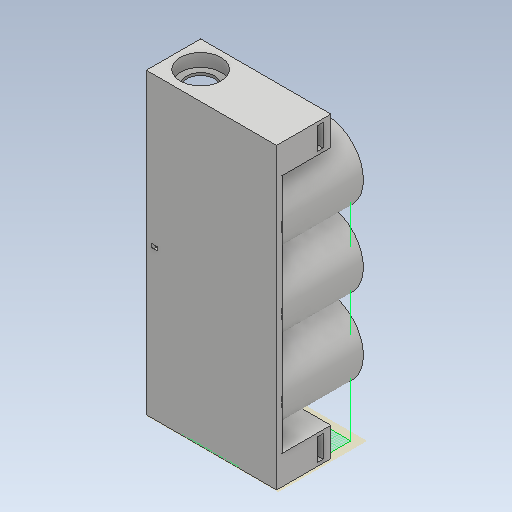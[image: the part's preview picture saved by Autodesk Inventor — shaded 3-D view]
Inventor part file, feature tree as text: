
AUTODESK INVENTOR PART (.ipt)
format: ipt  version: 2020 (Build 240168000, 168)  size: 739,328 bytes
history: native  units: mm
features: sketch x25, extrude x22, fillet x4
ambient origin geometry x8: Origin, YZ Plane, XZ Plane, XY Plane, X Axis, Y Axis, Z Axis, Center Point
bodies: Solid1 (feature_tree)
feature tree (51):
  extrude  "Extrusion1"  Depth=165.0mm
  extrude  "Extrusion2"  Depth=8.5mm
  extrude  "Extrusion3"  Depth=25.0mm TaperAngle=0.0deg
  extrude  "Extrusion4"  Depth=22.75mm
  extrude  "Extrusion5"  Depth=15.5mm
  extrude  "Extrusion6"  Depth=7.1mm TaperAngle=0.0deg
  fillet  "Fillet1"  Radius=5.0mm
  extrude  "Extrusion7"  Depth=10.0mm TaperAngle=0.0deg
  fillet  "Fillet2"  Radius=2.0mm
  extrude  "Extrusion8"  Depth=16.0mm
  extrude  "Extrusion9"  Depth=16.0mm
  fillet  "Fillet3"  Radius=8.0mm
  extrude  "Extrusion10"  Depth=6.0mm
  extrude  "Extrusion11"  Depth=12.25mm
  sketch  "Sketch12"  dims[d32=12.25mm d33=3.5mm]
  sketch  "Sketch13"  dims[d34=12.25mm d35=12.25mm]
  extrude  "Extrusion12"  Depth=12.25mm
  extrude  "Extrusion13"  Depth=12.25mm
  sketch  "Sketch16"  dims[d41=8.0mm d42=1.0mm]
  extrude  "Extrusion14"  Depth=40.0mm TaperAngle=0.0deg
  extrude  "Extrusion15"  Depth=2.0mm
  extrude  "Extrusion16"  Depth=1.0mm
  extrude  "Extrusion17"  Depth=2.0mm TaperAngle=0.0deg
  extrude  "Extrusion18"  Depth=7.1mm TaperAngle=0.0deg
  fillet  "Fillet4"  Radius=3.0mm
  extrude  "Extrusion19"  Depth=42.0mm
  extrude  "Extrusion20"  Depth=42.0mm
  extrude  "Extrusion21"  Depth=42.0mm
  extrude  "Extrusion22"  Depth=2.0mm
  sketch  "Sketch1"  dims[d0=25.0mm d1=165.0mm]
  sketch  "Sketch2"  dims[d2=3.0mm d3=0.0mm d4=8.5mm]
  sketch  "Sketch3"  dims[d5=8.5mm d6=25.0mm d7=0.0mm]
  sketch  "Sketch4"  dims[d8=25.0mm d9=22.75mm]
  sketch  "Sketch5"  dims[d10=7.1mm d11=0.0mm d12=15.5mm]
  sketch  "Sketch6"  dims[d13=165.0mm d14=0.0mm d15=7.1mm d16=0.0mm d17=5.0mm]
  sketch  "Sketch7"  dims[d18=5.0mm d19=10.0mm d20=0.0mm d21=2.0mm]
  sketch  "Sketch8"  dims[d22=16.0mm d23=8.0mm]
  sketch  "Sketch9"  dims[d24=16.0mm d25=16.0mm d26=8.0mm]
  sketch  "Sketch10"  dims[d27=45.0mm d28=0.0mm d29=6.0mm]
  sketch  "Sketch11"  dims[d30=12.25mm d31=3.5mm]
  sketch  "Sketch14"  dims[d36=3.5mm d37=40.0mm d38=0.0mm]
  sketch  "Sketch15"  dims[d39=1.0mm d40=2.0mm]
  sketch  "Sketch17"  dims[d43=2.0mm d44=12.0mm d45=0.0mm]
  sketch  "Sketch18"  dims[d46=6.0mm d47=7.1mm d48=0.0mm d49=3.0mm d50=0.0mm]
  sketch  "Sketch19"  dims[d51=42.0mm d52=38.75mm]
  sketch  "Sketch20"  dims[d53=42.0mm d54=38.75mm]
  sketch  "Sketch21"  dims[d55=42.0mm d56=38.75mm]
  sketch  "Sketch22"  dims[d57=45.0mm d58=0.0mm d59=2.0mm]
  sketch  "Sketch23"  dims[d60=4.0mm]
  sketch  "Sketch24"  dims[d61=2.0mm]
  sketch  "Sketch25"  dims[d62=4.0mm d63=45.0mm d64=0.0mm d65=10.0mm d66=12.0mm d67=0.0mm d68=2.0mm d69=0.0mm d70=2.0mm d71=0.0mm d72=2.0mm d73=2.0mm d74=5.0mm d75=0.0mm d76=2.0mm d77=2.0mm d78=7.0mm d79=0.0mm d80=1.0mm d81=0.25mm d82=0.25mm d83=44.75mm d84=0.0mm d85=44.0mm d86=0.0mm d87=22.6mm d88=8.5mm d89=0.0mm d90=22.6mm d91=8.5mm d92=0.0mm]
